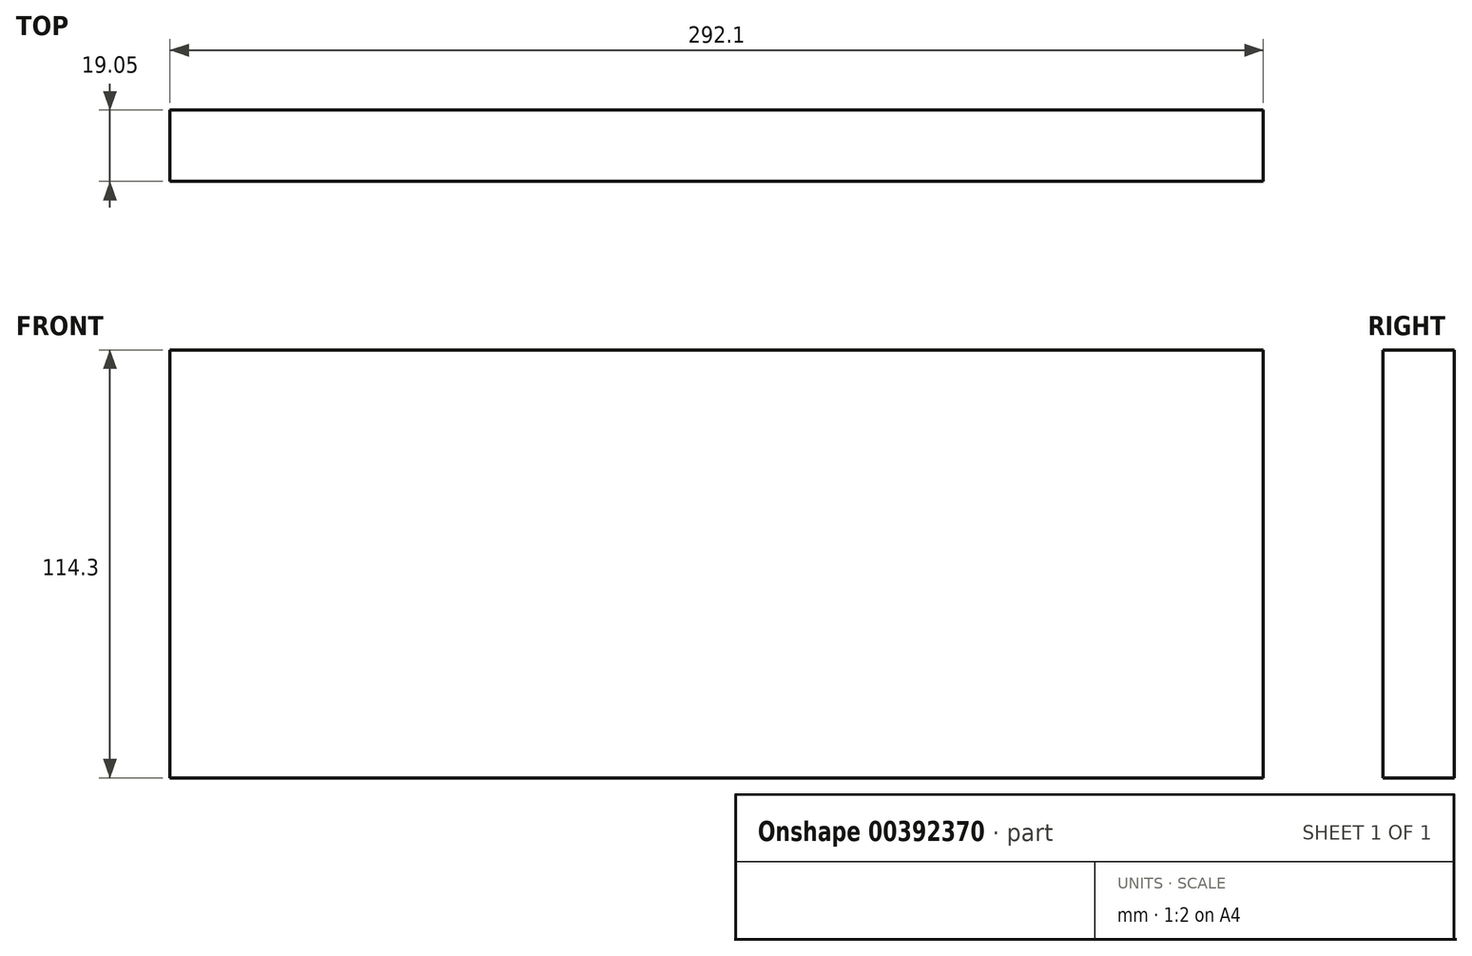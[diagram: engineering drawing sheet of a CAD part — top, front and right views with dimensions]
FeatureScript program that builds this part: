
annotation { "Feature Type Name" : "Feature", "Feature Type Description" : "" }
export const myFeature = defineFeature(function(context is Context, id is Id, definition is map)
    precondition{}
    {
        {
            var Q0;
            Q0=qCreatedBy(makeId("Front.planeOp"),FACE);
            var sketch = newSketch(context, id + "F0", { "sketchPlane" : qUnion([Q0])});
            skLineSegment(sketch, "E0.bottom", {"start": v(-123.86, 0) * mm, "end": v(168.24, 0) * mm});
            skLineSegment(sketch, "E0.top", {"start": v(-123.86, -114.3) * mm, "end": v(168.24, -114.3) * mm});
            skLineSegment(sketch, "E0.left", {"start": v(-123.86, 0) * mm, "end": v(-123.86, -114.3) * mm});
            skLineSegment(sketch, "E0.right", {"start": v(168.24, 0) * mm, "end": v(168.24, -114.3) * mm});
            skSolve(sketch);
        }
        {
            var Q0;
            Q0=makeQuery(id+"F0.imprint","IMPRINT",FACE,{"disambiguationData":[TD([[makeQuery(id+"F0.imprint","IMPRINT",EDGE,{"derivedFrom":sQuery(id+"F0.wireOp",EDGE,"E0.bottom")}),-1.0]])]});
            extrude(context, id + "F1", {"entities" : qUnion([Q0]), "depth" : 19.05 * mm});
        }
    });
